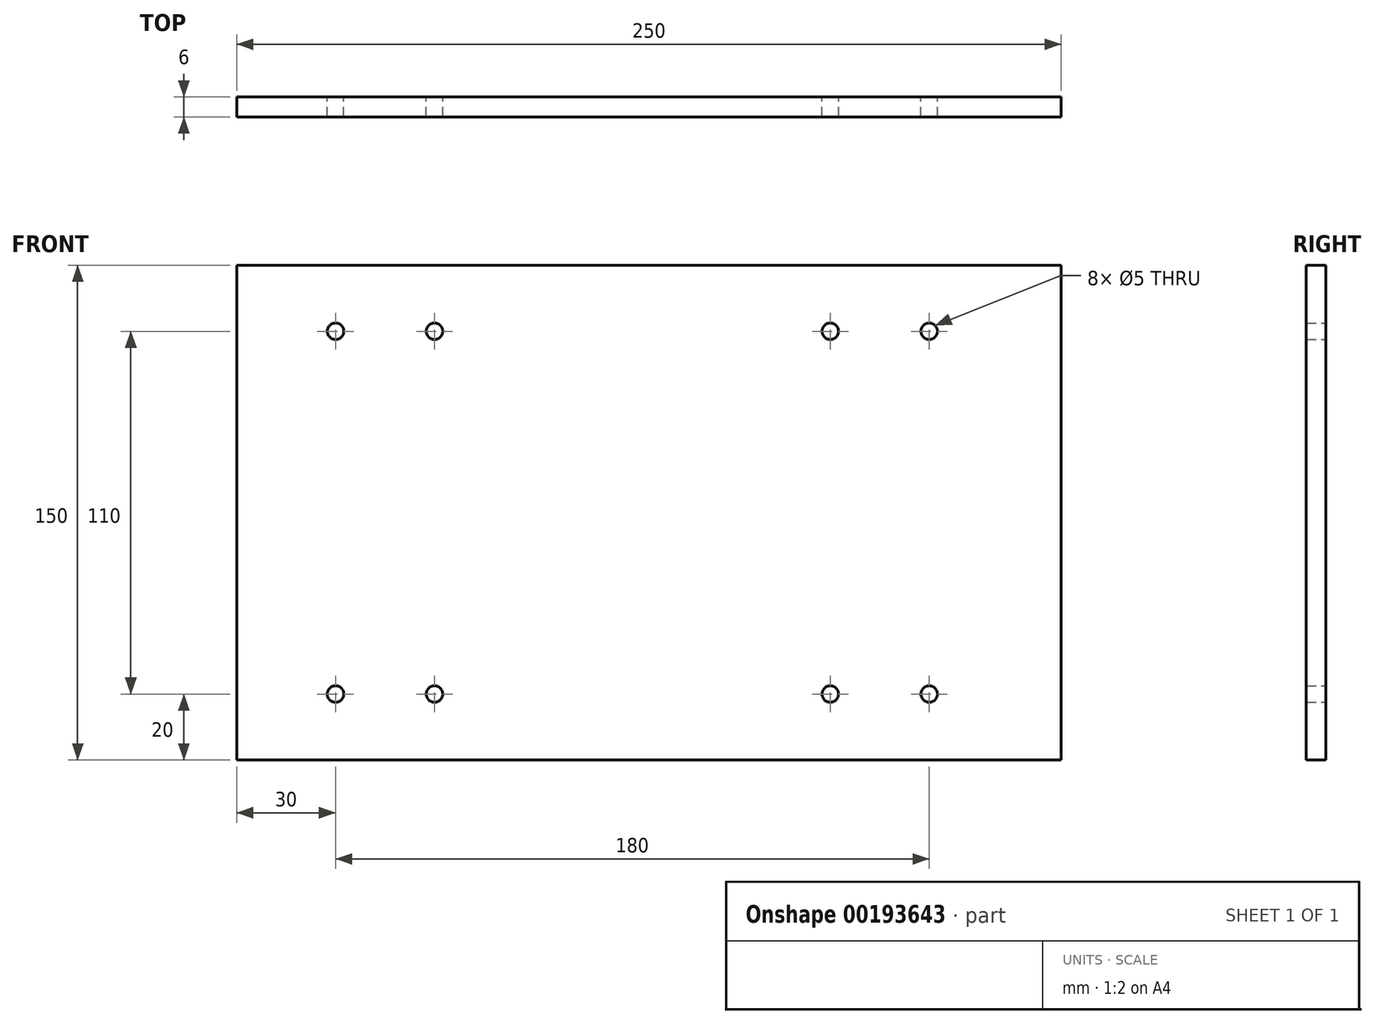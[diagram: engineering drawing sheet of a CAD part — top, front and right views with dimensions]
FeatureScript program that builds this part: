
annotation { "Feature Type Name" : "Feature", "Feature Type Description" : "" }
export const myFeature = defineFeature(function(context is Context, id is Id, definition is map)
    precondition{}
    {
        {
            var Q0;
            Q0=qCreatedBy(makeId("Front.planeOp"),FACE);
            var sketch = newSketch(context, id + "F0", { "sketchPlane" : qUnion([Q0])});
            skLineSegment(sketch, "E0.bottom", {"start": v(-125, 75) * mm, "end": v(125, 75) * mm});
            skLineSegment(sketch, "E0.top", {"start": v(-125, -75) * mm, "end": v(125, -75) * mm});
            skLineSegment(sketch, "E0.left", {"start": v(-125, 75) * mm, "end": v(-125, -75) * mm});
            skLineSegment(sketch, "E0.right", {"start": v(125, 75) * mm, "end": v(125, -75) * mm});
            skPoint(sketch, "E0.middle", {"position": v(0, 0) * mm});
            skCircle(sketch, "E1", {"center": v(-95, 55) * mm, "radius": 2.5 * mm});
            skCircle(sketch, "E2", {"center": v(-65, 55) * mm, "radius": 2.5 * mm});
            skCircle(sketch, "E3", {"center": v(55, 55) * mm, "radius": 2.5 * mm});
            skCircle(sketch, "E4", {"center": v(85, 55) * mm, "radius": 2.5 * mm});
            skCircle(sketch, "E5", {"center": v(-95, -55) * mm, "radius": 2.5 * mm});
            skCircle(sketch, "E6", {"center": v(-65, -55) * mm, "radius": 2.5 * mm});
            skCircle(sketch, "E7", {"center": v(55, -55) * mm, "radius": 2.5 * mm});
            skCircle(sketch, "E8", {"center": v(85, -55) * mm, "radius": 2.5 * mm});
            skSolve(sketch);
        }
        {
            var Q0;
            Q0=makeQuery(id+"F0.imprint","IMPRINT",FACE,{"disambiguationData":[TD([[makeQuery(id+"F0.imprint","IMPRINT",EDGE,{"derivedFrom":sQuery(id+"F0.wireOp",EDGE,"E0.bottom")}),-1.0]])]});
            extrude(context, id + "F1", {"entities" : qUnion([Q0]), "depth" : 6 * mm});
        }
    });
